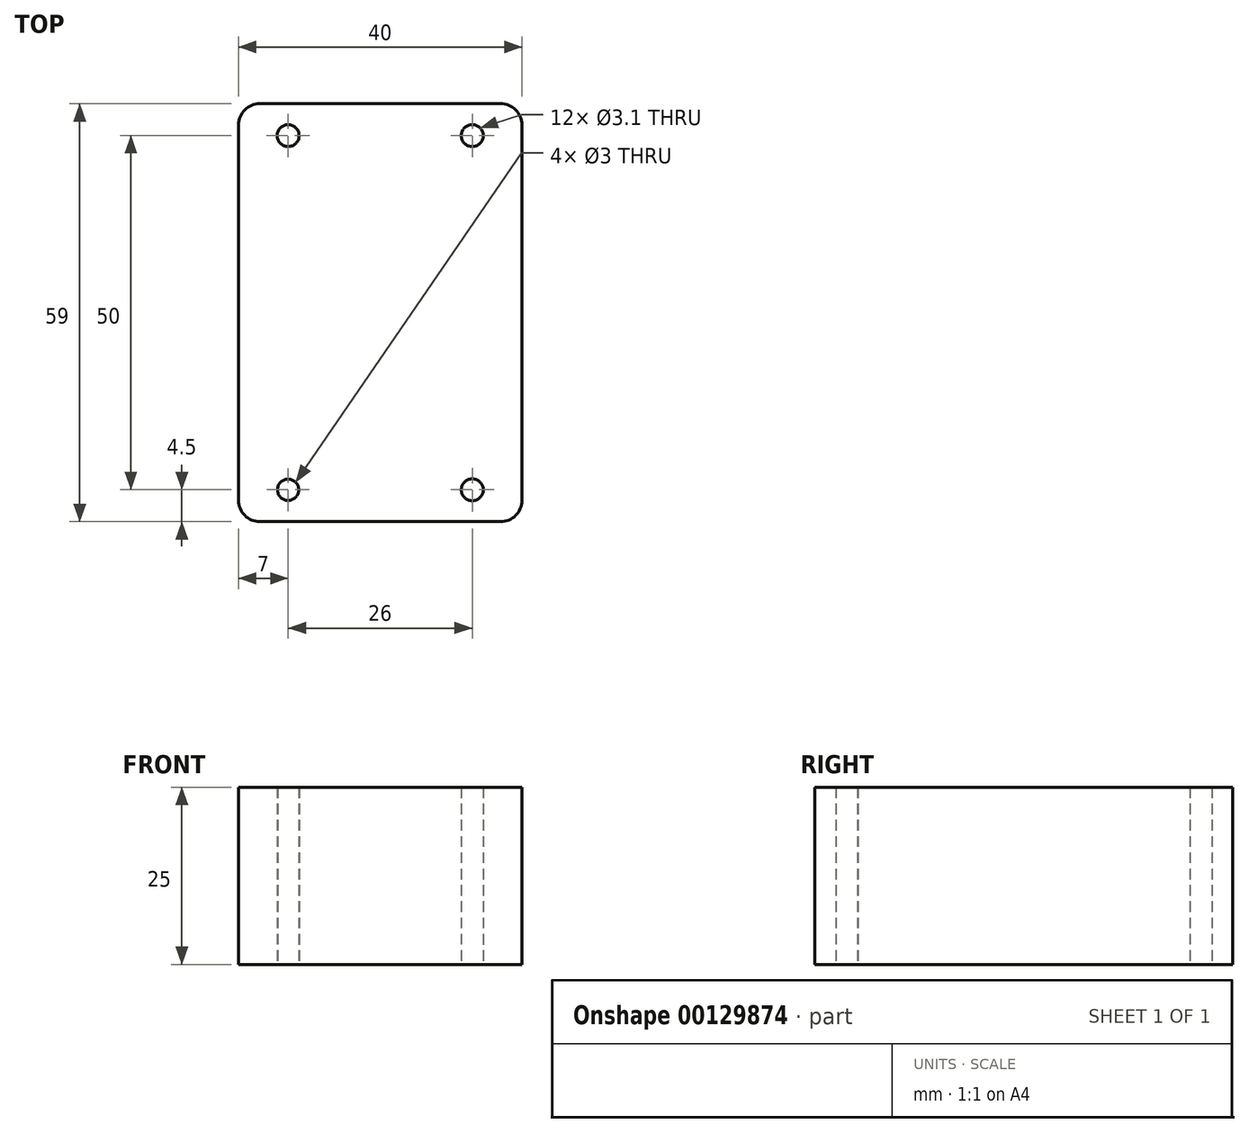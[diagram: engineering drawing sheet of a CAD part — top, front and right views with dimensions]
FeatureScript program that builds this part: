
annotation { "Feature Type Name" : "Feature", "Feature Type Description" : "" }
export const myFeature = defineFeature(function(context is Context, id is Id, definition is map)
    precondition{}
    {
        {
            var Q0;
            Q0=qCreatedBy(makeId("Top.planeOp"),FACE);
            var sketch = newSketch(context, id + "F0", { "sketchPlane" : qUnion([Q0])});
            skLineSegment(sketch, "E0.bottom", {"start": v(13, 25) * mm, "end": v(-13, 25) * mm});
            skLineSegment(sketch, "E0.top", {"start": v(13, -25) * mm, "end": v(-13, -25) * mm});
            skLineSegment(sketch, "E0.left", {"start": v(13, 25) * mm, "end": v(13, -25) * mm});
            skLineSegment(sketch, "E0.right", {"start": v(-13, 25) * mm, "end": v(-13, -25) * mm});
            skPoint(sketch, "E0.middle", {"position": v(0, 0) * mm});
            skCircle(sketch, "E1", {"center": v(13, 25) * mm, "radius": 1.55 * mm});
            skCircle(sketch, "E2", {"center": v(-13, 25) * mm, "radius": 1.55 * mm});
            skCircle(sketch, "E3", {"center": v(13, -25) * mm, "radius": 1.55 * mm});
            skCircle(sketch, "E4", {"center": v(-13, -25) * mm, "radius": 1.5 * mm});
            skLineSegment(sketch, "E5.bottom", {"start": v(20, 29.5) * mm, "end": v(-20, 29.5) * mm});
            skLineSegment(sketch, "E5.top", {"start": v(20, -29.5) * mm, "end": v(-20, -29.5) * mm});
            skLineSegment(sketch, "E5.left", {"start": v(20, 29.5) * mm, "end": v(20, -29.5) * mm});
            skLineSegment(sketch, "E5.right", {"start": v(-20, 29.5) * mm, "end": v(-20, -29.5) * mm});
            skSolve(sketch);
        }
        {
            var Q0;
            Q0=makeQuery(id+"F0.imprint","IMPRINT",FACE,{"disambiguationData":[TD([[makeQuery(id+"F0.imprint","IMPRINT",EDGE,{"derivedFrom":sQuery(id+"F0.wireOp",EDGE,"E5.bottom")}),1.0]])]});
            var Q1;
            {var subQ5=sQuery(id+"F0.wireOp",EDGE,"E1");var subQ13=sQuery(id+"F0.wireOp",EDGE,"E0.bottom");var subQ14=makeQuery(id+"F0.imprint","INTERSECT",VERTEX,{"derivedFrom":[subQ13,subQ5]});Q1=makeQuery(id+"F0.imprint","IMPRINT",FACE,{"disambiguationData":[TD([[makeQuery(id+"F0.imprint","IMPRINT",EDGE,{"disambiguationData":[TD([[subQ14,-1.0]])],"derivedFrom":subQ13}),1.0]])]});}
            extrude(context, id + "F1", {"entities" : qUnion([Q0, Q1]), "depth" : 25 * mm});
        }
        {
            var Q0;
            Q0=makeQuery(id+"F1.opExtrude","SWEPT_EDGE",EDGE,{"disambiguationData":[OSD([sQuery(id+"F0.wireOp",EDGE,"E5.bottom"),sQuery(id+"F0.wireOp",EDGE,"E5.right")])]});
            var Q1;
            Q1=makeQuery(id+"F1.opExtrude","SWEPT_EDGE",EDGE,{"disambiguationData":[OSD([sQuery(id+"F0.wireOp",EDGE,"E5.bottom"),sQuery(id+"F0.wireOp",EDGE,"E5.left")])]});
            var Q2;
            Q2=makeQuery(id+"F1.opExtrude","SWEPT_EDGE",EDGE,{"disambiguationData":[OSD([sQuery(id+"F0.wireOp",EDGE,"E5.top"),sQuery(id+"F0.wireOp",EDGE,"E5.left")])]});
            var Q3;
            Q3=makeQuery(id+"F1.opExtrude","SWEPT_EDGE",EDGE,{"disambiguationData":[OSD([sQuery(id+"F0.wireOp",EDGE,"E5.top"),sQuery(id+"F0.wireOp",EDGE,"E5.right")])]});
            fillet(context, id + "F2", {"entities" : qUnion([Q0, Q1, Q2, Q3]), "radius" : 3 * mm, "tangentPropagation" : true, "allowEdgeOverflow" : false});
        }
    });
